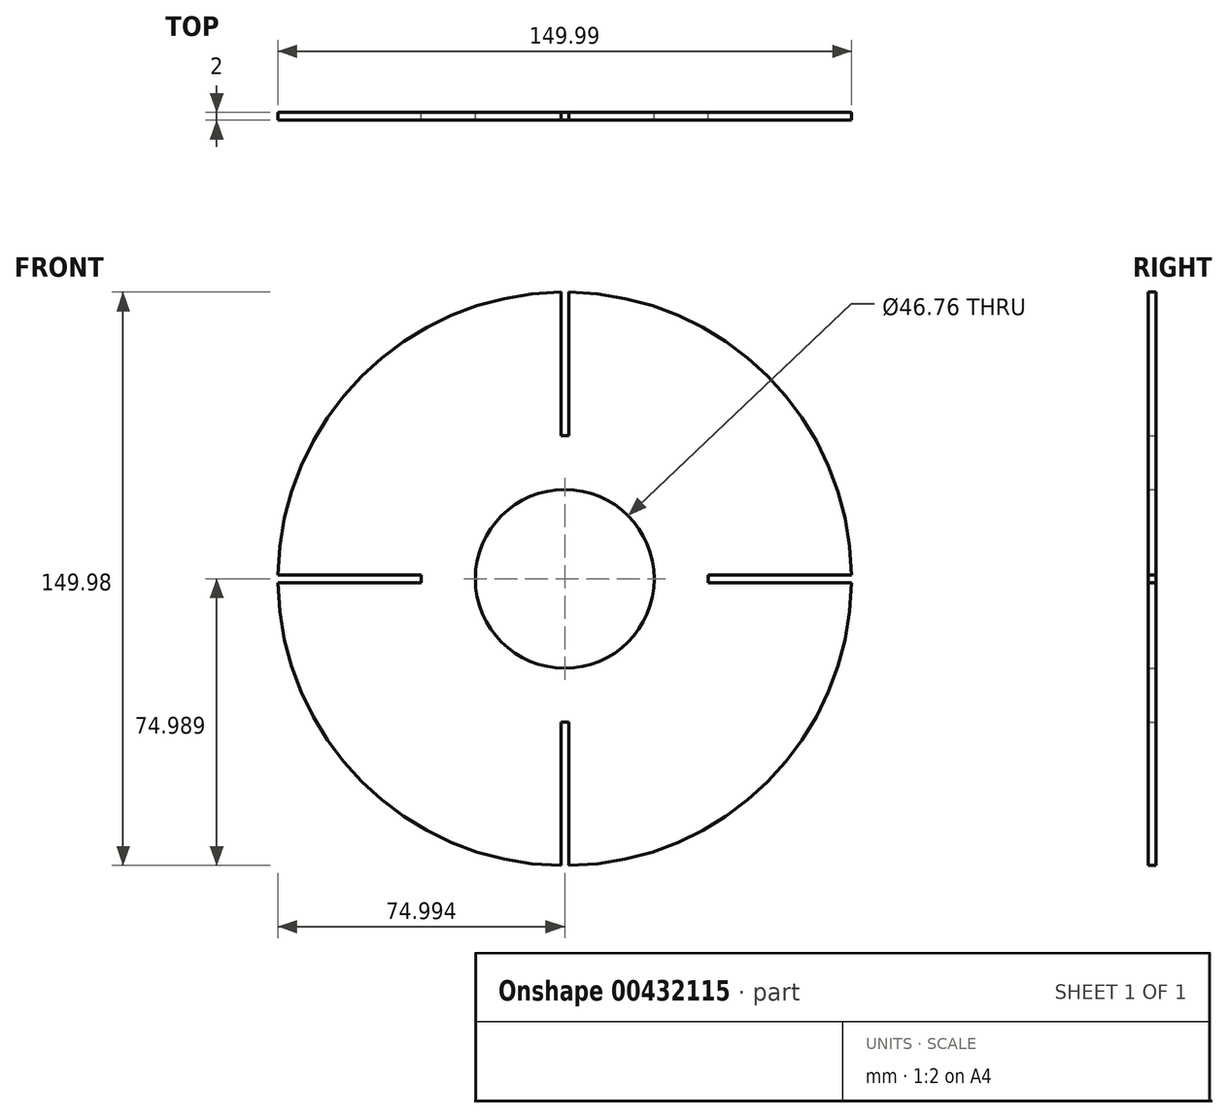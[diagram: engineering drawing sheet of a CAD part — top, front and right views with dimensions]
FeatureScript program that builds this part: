
annotation { "Feature Type Name" : "Feature", "Feature Type Description" : "" }
export const myFeature = defineFeature(function(context is Context, id is Id, definition is map)
    precondition{}
    {
        {
            var Q0;
            Q0=qCreatedBy(makeId("Front.planeOp"),FACE);
            var sketch = newSketch(context, id + "F0", { "sketchPlane" : qUnion([Q0])});
            skArc(sketch, "E0", {"start": v(-309.55, 126.78) * mm, "mid": v(-361.58, 104.82) * mm, "end": v(-383.54, 52.79) * mm});
            skLineSegment(sketch, "E1.MirrorCS", {"start": v(-309.55, 126.79) * mm, "end": v(-309.55, 89.29) * mm});
            skLineSegment(sketch, "E2", {"start": v(-309.55, 89.29) * mm, "end": v(-307.55, 89.29) * mm});
            skLineSegment(sketch, "E3.top", {"start": v(-383.55, 52.79) * mm, "end": v(-346.05, 52.79) * mm});
            skLineSegment(sketch, "E3.right", {"start": v(-346.05, 51.79) * mm, "end": v(-346.05, 52.79) * mm});
            skPoint(sketch, "E4.trimOffspring.start.orphan", {"position": v(-383.55, 51.79) * mm});
            skLineSegment(sketch, "E5.MirrorCS", {"start": v(-271.05, 51.79) * mm, "end": v(-271.05, 52.79) * mm});
            skLineSegment(sketch, "E6.MirrorCS", {"start": v(-307.55, 89.29) * mm, "end": v(-309.55, 89.29) * mm});
            skArc(sketch, "E7.MirrorCS", {"start": v(-307.55, 126.78) * mm, "mid": v(-255.51, 104.82) * mm, "end": v(-233.55, 52.79) * mm});
            skLineSegment(sketch, "E8.MirrorCS", {"start": v(-233.55, 52.79) * mm, "end": v(-271.05, 52.79) * mm});
            skPoint(sketch, "E9.MirrorP", {"position": v(-233.55, 51.79) * mm});
            skLineSegment(sketch, "E10.MirrorCS", {"start": v(-307.55, 126.79) * mm, "end": v(-307.55, 89.29) * mm});
            skLineSegment(sketch, "E11.MirrorCS", {"start": v(-309.55, 14.29) * mm, "end": v(-307.55, 14.29) * mm});
            skLineSegment(sketch, "E12.MirrorCS", {"start": v(-307.55, 14.29) * mm, "end": v(-309.55, 14.29) * mm});
            skLineSegment(sketch, "E13.MirrorCS", {"start": v(-271.05, 51.79) * mm, "end": v(-271.05, 50.79) * mm});
            skLineSegment(sketch, "E14.MirrorCS", {"start": v(-346.05, 51.79) * mm, "end": v(-346.05, 50.79) * mm});
            skLineSegment(sketch, "E15.MirrorCS", {"start": v(-383.55, 50.79) * mm, "end": v(-346.05, 50.79) * mm});
            skLineSegment(sketch, "E16.MirrorCS", {"start": v(-233.55, 50.79) * mm, "end": v(-271.05, 50.79) * mm});
            skLineSegment(sketch, "E17.MirrorCS", {"start": v(-307.55, -23.21) * mm, "end": v(-307.55, 14.29) * mm});
            skArc(sketch, "E18.MirrorCS", {"start": v(-307.55, -23.2) * mm, "mid": v(-255.51, -1.24) * mm, "end": v(-233.55, 50.79) * mm});
            skLineSegment(sketch, "E19.MirrorCS", {"start": v(-309.55, -23.21) * mm, "end": v(-309.55, 14.29) * mm});
            skArc(sketch, "E20.MirrorCS", {"start": v(-309.55, -23.2) * mm, "mid": v(-361.58, -1.24) * mm, "end": v(-383.54, 50.79) * mm});
            skPoint(sketch, "E21.MirrorCS.end.orphan", {"position": v(-308.55, 89.29) * mm});
            skPoint(sketch, "E22.MirrorCS.end.orphan", {"position": v(-308.55, 14.29) * mm});
            skCircle(sketch, "E23", {"center": v(-308.55, 51.79) * mm, "radius": 23.38 * mm});
            skSolve(sketch);
        }
        {
            var Q0;
            {var subQ6=sQuery(id+"F0.wireOp",EDGE,"E0");Q0=makeQuery(id+"F0.imprint","IMPRINT",FACE,{"disambiguationData":[TD([[makeQuery(id+"F0.imprint","IMPRINT",EDGE,{"derivedFrom":subQ6}),1.0]])]});}
            extrude(context, id + "F1", {"entities" : qUnion([Q0]), "depth" : 2 * mm});
        }
    });
